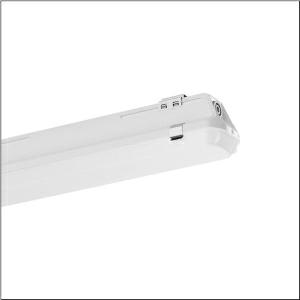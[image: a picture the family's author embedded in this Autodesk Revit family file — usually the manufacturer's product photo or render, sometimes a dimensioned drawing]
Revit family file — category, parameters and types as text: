
# Revit family: monsun_r__21_parking_51fg20dp440bhr_9634
name_source: partatom
category: Lighting Fixtures
units: mm (PartAtom-declared; Revit-internal decimal feet)

## family parameters
Cut with Voids When Loaded = No
Host = Face
Light Source = No
Part Type = Normal
Room Calculation Point = No
Round Connector Dimension = Use Diameter
Shared = No

## types (1)
- --- (1 x LED, 4810 lm, 34.9 W, 4000K)
    Apparent Load = 35 VA
    CIE Flux Codes = 45 75 93 94 100
    Color Rendering = 80
    Color Temperature = 4000K
    Default Elevation = 1800 mm
    Description = Monsun® 21 parking, damp-proof luminaire, chain hanger, primary optical cover: enclosure, of PC, light emission: direct distribution, primary light characteristic: symmetric, installation type: vertical mounting, horizontal mounting, surface-mounted, suspended mounting, LED, rated luminous flux: 4.810lm, luminous efficacy: 140lm/W, light colour: 840, colour temperature: 4000K, control gear: ECG DALI, with terminal, 5-pole, max. 2.5mm², mains connection: 220..240V, AC, 50/60Hz, rated input power: 34W, housing, of glass-fibre reinforced polyester, uncoated, bright grey, incl. chain hanger, length: 1.590mm, width: 90mm, height: 88mm, clip for enclosure, of stainless steel (V2A), ceiling mounting element, of stainless steel (V2A), chain hanger, of stainless steel (V2A), multi-sensor HC1, local control, light sensor deactivated, dimmable, protection rating (complete): IP66, insulation class (complete): insulation class I (protective earthing), certification: CE, ENEC, VDE, UKCA, protection symbol: D, impact resistance: IK08, permissible operating ambient temperature: -25..+35°C, standard: EN 50419, EN 60598-2-1, no direct snow, no direct sun, no direct rain, for indoor or canopied outdoor use, corresponds to IFS (International Featured Standards) requirements for safety and quality in the food industry, contact your sales advisor before using the luminaires in applications with unclear chemical exposure, large temperature fluctuations or condensation-forming humidity, LABS conformity tested according to VDMA 24364:2018-05, packaging unit: 1 piece
    Height = 89 mm
    Lamp = 1 x LED
    Lamp Light Flux = 4810 lm
    Lamp Power = 34.9 W
    Lamp count = 1
    Length = 1590 mm
    Luminous efficacy = 138 lm/W
    Manufacturer = Siteco
    ModVariant = No
    Model = 51FG20DP440BHR
    Mounting Place = Ceiling
    Mounting Type = Surface mounted
    Number of Poles = 1
    OnlyDefault = Yes
    Power Factor = 1
    Product Name = Monsun® 21 parking
    Product group = damp-proof luminaire
    ProductGroupID = 301
    Protection Class = Protection class I
    Protection Degree = IP 66
    RLX_Detail_Level = 1
    RLX_Emergency_Light_Flux = 0 lm
    RLX_Emergency_Type = 0
    RLX_Emergency_Type_DB = No
    RlxData = <blob elided: 92717 chars, md5=fbaaa692>
    Socket = socket
    Standby Power = 0 W
    System Light Flux = 4810 lm
    System Power = 35 W
    Type Comments = factory setting: luminous flux: 100 % | dim-lin: 254 | 228 mA
    Type Image = l_1006717.jpg
    URL = http://relux.com
    VarID = @adj_092797
    Voltage = 0 V
    Weight = 0.00 kg
    Width = 90 mm

## geometry (parser evidence)
native form markers: Blend x4, Sweep x14
no freeform markers — native parametric forms only
